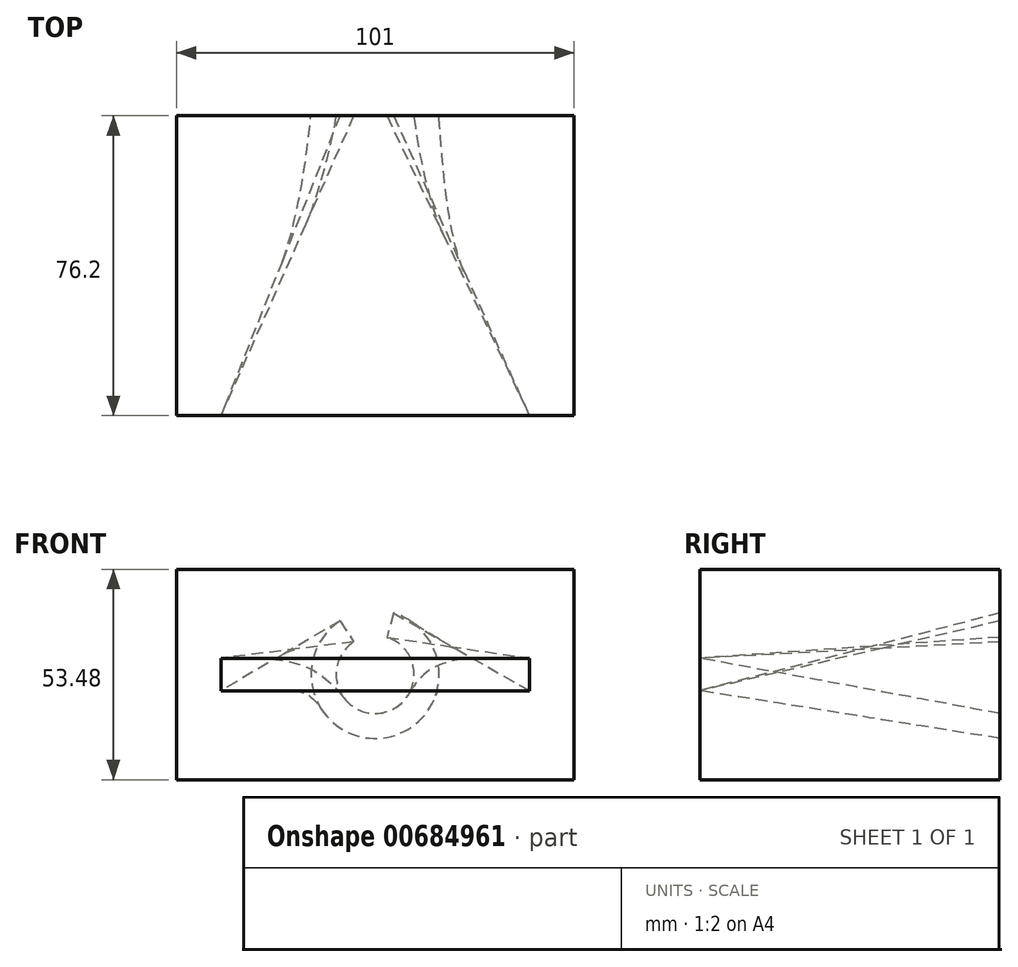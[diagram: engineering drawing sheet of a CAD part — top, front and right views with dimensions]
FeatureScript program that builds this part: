
annotation { "Feature Type Name" : "Feature", "Feature Type Description" : "" }
export const myFeature = defineFeature(function(context is Context, id is Id, definition is map)
    precondition{}
    {
        {
            var Q0;
            Q0=qCreatedBy(makeId("Front.planeOp"),FACE);
            var sketch = newSketch(context, id + "F0", { "sketchPlane" : qUnion([Q0])});
            skArc(sketch, "E0", {"start": v(-5.45, 8.28) * mm, "mid": v(1.36, -9.82) * mm, "end": v(2.99, 9.45) * mm});
            skArc(sketch, "E1.0", {"start": v(-8.94, 13.58) * mm, "mid": v(2.37, -16.09) * mm, "end": v(4.65, 15.58) * mm});
            skLineSegment(sketch, "E2", {"start": v(-8.94, 13.58) * mm, "end": v(-5.45, 8.28) * mm});
            skLineSegment(sketch, "E3", {"start": v(4.65, 15.58) * mm, "end": v(2.99, 9.45) * mm});
            skSolve(sketch);
        }
        {
            var Q0;
            Q0=qCreatedBy(makeId("Front.planeOp"),FACE);
            cPlane(context, id + "F1", {"entities" : qUnion([Q0]), "cplaneType" : CPlaneType.OFFSET, "offset" : 76.2 * mm, "width" : 152.4 * mm, "height" : 152.4 * mm});
        }
        {
            var Q0;
            Q0=qCreatedBy(id+"F1.planeOp",FACE);
            var sketch = newSketch(context, id + "F2", { "sketchPlane" : qUnion([Q0])});
            skLineSegment(sketch, "E4.bottom", {"start": v(-39.21, 4.12) * mm, "end": v(39.21, 4.12) * mm});
            skLineSegment(sketch, "E4.top", {"start": v(-39.21, -4.12) * mm, "end": v(39.21, -4.12) * mm});
            skLineSegment(sketch, "E4.left", {"start": v(-39.21, 4.12) * mm, "end": v(-39.21, -4.12) * mm});
            skLineSegment(sketch, "E4.right", {"start": v(39.21, 4.12) * mm, "end": v(39.21, -4.12) * mm});
            skPoint(sketch, "E4.middle", {"position": v(0, 0) * mm});
            skSolve(sketch);
        }
        {
            var Q0;
            Q0=makeQuery(id+"F0.imprint","IMPRINT",FACE,{"disambiguationData":[TD([[makeQuery(id+"F0.imprint","IMPRINT",EDGE,{"derivedFrom":sQuery(id+"F0.wireOp",EDGE,"E0")}),-1.0]])]});
            var Q1;
            Q1=makeQuery(id+"F2.imprint","IMPRINT",FACE,{"disambiguationData":[TD([[makeQuery(id+"F2.imprint","IMPRINT",EDGE,{"derivedFrom":sQuery(id+"F2.wireOp",EDGE,"E4.bottom")}),-1.0]])]});
            var Q2;
            Q2=makeQuery(id+"F0.imprint","IMPRINT",FACE,{"disambiguationData":[TD([[makeQuery(id+"F0.imprint","IMPRINT",EDGE,{"derivedFrom":sQuery(id+"F0.wireOp",EDGE,"E0")}),-1.0]])]});
            var Q3;
            Q3=makeQuery(id+"F2.imprint","IMPRINT",FACE,{"disambiguationData":[TD([[makeQuery(id+"F2.imprint","IMPRINT",EDGE,{"derivedFrom":sQuery(id+"F2.wireOp",EDGE,"E4.bottom")}),-1.0]])]});
            loft(context, id + "F3", {"sheetProfilesArray" : [{ "sheetProfileEntities" : qUnion([Q0]) }, { "sheetProfileEntities" : qUnion([Q1]) }], "wireProfilesArray" : [{ "wireProfileEntities" : qUnion([Q2]) }, { "wireProfileEntities" : qUnion([Q3]) }]});
        }
        {
            var Q0;
            Q0=qCreatedBy(makeId("Front.planeOp"),FACE);
            var sketch = newSketch(context, id + "F4", { "sketchPlane" : qUnion([Q0])});
            skLineSegment(sketch, "E5.bottom", {"start": v(50.5, 26.74) * mm, "end": v(-50.5, 26.74) * mm});
            skLineSegment(sketch, "E5.top", {"start": v(50.5, -26.74) * mm, "end": v(-50.5, -26.74) * mm});
            skLineSegment(sketch, "E5.left", {"start": v(50.5, 26.74) * mm, "end": v(50.5, -26.74) * mm});
            skLineSegment(sketch, "E5.right", {"start": v(-50.5, 26.74) * mm, "end": v(-50.5, -26.74) * mm});
            skPoint(sketch, "E5.middle", {"position": v(0, 0) * mm});
            skSolve(sketch);
        }
        {
            var Q0;
            Q0=qSketchRegion(id+"F4",true);
            extrude(context, id + "F5", {"entities" : qUnion([Q0]), "depth" : 76.2 * mm});
        }
        {
            var Q0;
            Q0=qCreatedBy(makeId("Front.planeOp"),FACE);
            var sketch = newSketch(context, id + "F6", { "sketchPlane" : qUnion([Q0])});
            skLineSegment(sketch, "E6", {"start": v(16.06, 0) * mm, "end": v(10.13, 0) * mm});
            skSolve(sketch);
        }
        {
            var Q0;
            Q0=qCreatedBy(id+"F1.planeOp",FACE);
            var sketch = newSketch(context, id + "F7", { "sketchPlane" : qUnion([Q0])});
            skPoint(sketch, "E7", {"position": v(3.05, 5.57) * mm});
            skSolve(sketch);
        }
    });
